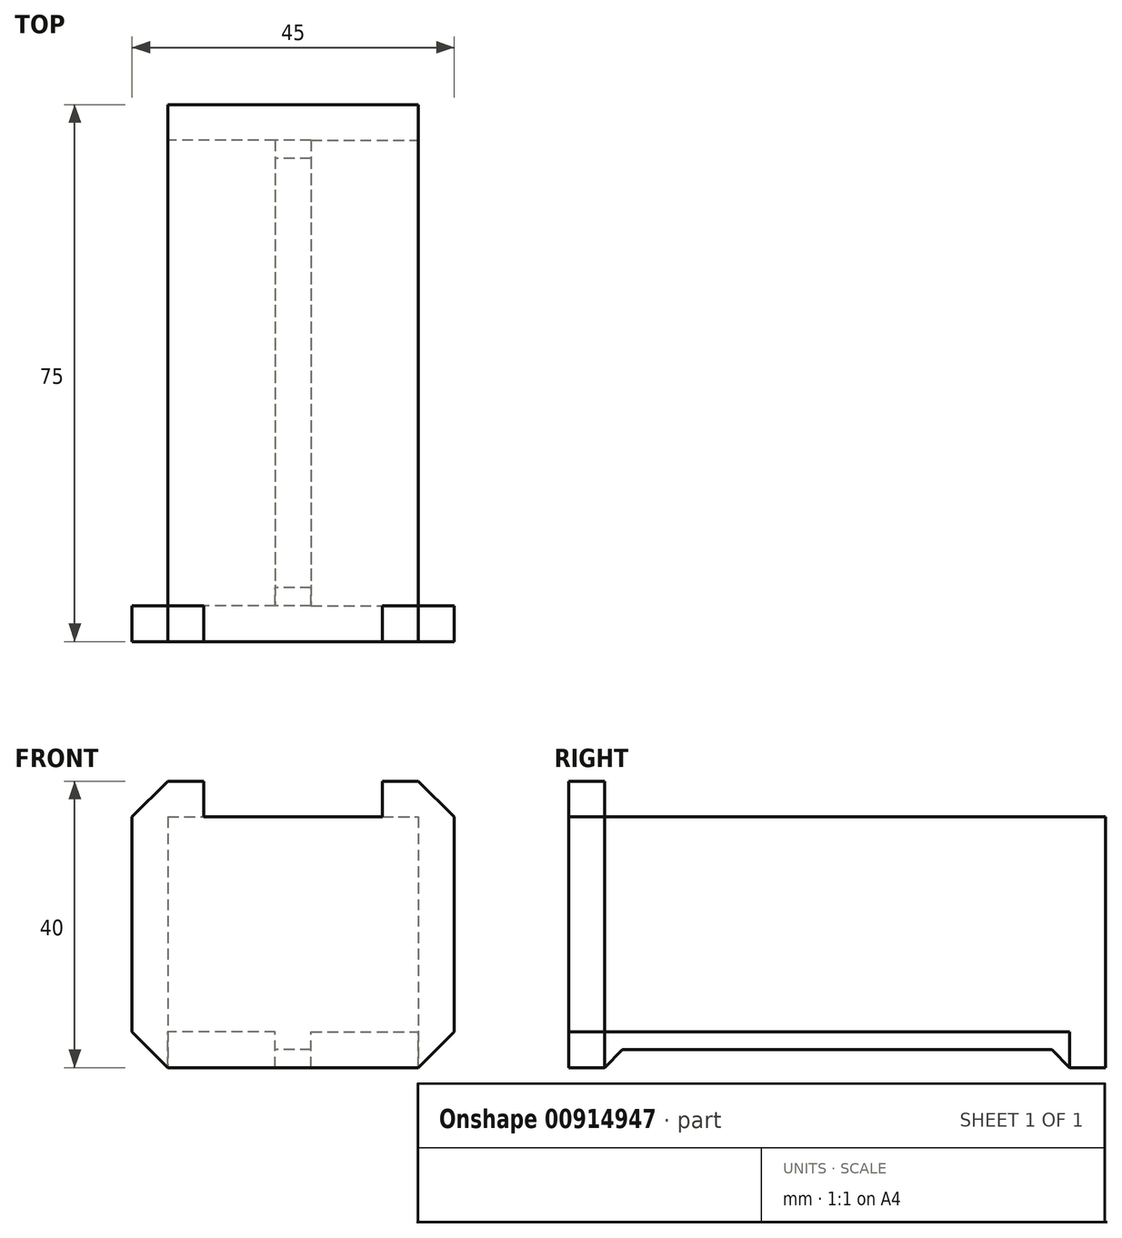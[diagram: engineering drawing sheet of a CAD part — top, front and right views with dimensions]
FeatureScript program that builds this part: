
annotation { "Feature Type Name" : "Feature", "Feature Type Description" : "" }
export const myFeature = defineFeature(function(context is Context, id is Id, definition is map)
    precondition{}
    {
        {
            var Q0;
            Q0=qCreatedBy(makeId("Top.planeOp"),FACE);
            var sketch = newSketch(context, id + "F0", { "sketchPlane" : qUnion([Q0])});
            skLineSegment(sketch, "E0", {"start": v(0, 0) * mm, "end": v(17.5, 0) * mm});
            skLineSegment(sketch, "E1.MirrorCS", {"start": v(0, 0) * mm, "end": v(-17.5, 0) * mm});
            skLineSegment(sketch, "E2", {"start": v(-17.5, 37.5) * mm, "end": v(-17.5, -37.5) * mm});
            skLineSegment(sketch, "E3.MirrorCS", {"start": v(17.5, 37.5) * mm, "end": v(17.5, -37.5) * mm});
            skLineSegment(sketch, "E4", {"start": v(-17.5, -37.5) * mm, "end": v(17.5, -37.5) * mm});
            skLineSegment(sketch, "E5", {"start": v(-17.5, 37.5) * mm, "end": v(17.5, 37.5) * mm});
            skLineSegment(sketch, "E6", {"start": v(0, 37.5) * mm, "end": v(-2.5, 37.5) * mm});
            skLineSegment(sketch, "E7", {"start": v(-2.5, 37.5) * mm, "end": v(-2.5, -37.5) * mm});
            skLineSegment(sketch, "E8.MirrorCS", {"start": v(2.5, 37.5) * mm, "end": v(2.5, -37.5) * mm});
            skLineSegment(sketch, "E9", {"start": v(2.5, 32.5) * mm, "end": v(-2.5, 32.5) * mm});
            skLineSegment(sketch, "E10", {"start": v(-17.5, -37.5) * mm, "end": v(-22.5, -37.5) * mm});
            skLineSegment(sketch, "E11.MirrorCS", {"start": v(2.5, -32.5) * mm, "end": v(-2.5, -32.5) * mm});
            skLineSegment(sketch, "E12", {"start": v(-2.5, -32.5) * mm, "end": v(-22.5, -32.5) * mm});
            skLineSegment(sketch, "E13", {"start": v(-22.5, -32.5) * mm, "end": v(-22.5, -37.5) * mm});
            skLineSegment(sketch, "E14.MirrorCS", {"start": v(2.5, -32.5) * mm, "end": v(22.5, -32.5) * mm});
            skLineSegment(sketch, "E15.MirrorCS", {"start": v(22.5, -32.5) * mm, "end": v(22.5, -37.5) * mm});
            skLineSegment(sketch, "E16.MirrorCS", {"start": v(17.5, -37.5) * mm, "end": v(22.5, -37.5) * mm});
            skLineSegment(sketch, "E17.MirrorCS", {"start": v(-2.5, 32.5) * mm, "end": v(-22.5, 32.5) * mm});
            skLineSegment(sketch, "E18.MirrorCS", {"start": v(-22.5, 32.5) * mm, "end": v(-22.5, 37.5) * mm});
            skLineSegment(sketch, "E19.MirrorCS", {"start": v(-17.5, 37.5) * mm, "end": v(-22.5, 37.5) * mm});
            skLineSegment(sketch, "E20.MirrorCS", {"start": v(2.5, 32.5) * mm, "end": v(22.5, 32.5) * mm});
            skLineSegment(sketch, "E21.MirrorCS", {"start": v(17.5, 37.5) * mm, "end": v(22.5, 37.5) * mm});
            skLineSegment(sketch, "E22.MirrorCS", {"start": v(22.5, 32.5) * mm, "end": v(22.5, 37.5) * mm});
            skSolve(sketch);
        }
        {
            var Q0;
            {var subQ3=sQuery(id+"F0.wireOp",EDGE,"E1.MirrorCS");Q0=makeQuery(id+"F0.imprint","IMPRINT",FACE,{"disambiguationData":[TD([[makeQuery(id+"F0.imprint","IMPRINT",EDGE,{"derivedFrom":subQ3}),-1.0]])]});}
            var Q1;
            {var subQ3=sQuery(id+"F0.wireOp",EDGE,"E1.MirrorCS");Q1=makeQuery(id+"F0.imprint","IMPRINT",FACE,{"disambiguationData":[TD([[makeQuery(id+"F0.imprint","IMPRINT",EDGE,{"derivedFrom":subQ3}),1.0]])]});}
            var Q2;
            {var subQ3=sQuery(id+"F0.wireOp",EDGE,"E0");Q2=makeQuery(id+"F0.imprint","IMPRINT",FACE,{"disambiguationData":[TD([[makeQuery(id+"F0.imprint","IMPRINT",EDGE,{"derivedFrom":subQ3}),1.0]])]});}
            var Q3;
            {var subQ3=sQuery(id+"F0.wireOp",EDGE,"E0");Q3=makeQuery(id+"F0.imprint","IMPRINT",FACE,{"disambiguationData":[TD([[makeQuery(id+"F0.imprint","IMPRINT",EDGE,{"derivedFrom":subQ3}),-1.0]])]});}
            var Q4;
            {var subQ0=sQuery(id+"F0.wireOp",EDGE,"E6");Q4=makeQuery(id+"F0.imprint","IMPRINT",FACE,{"disambiguationData":[TD([[makeQuery(id+"F0.imprint","IMPRINT",EDGE,{"derivedFrom":subQ0}),1.0]])]});}
            var Q5;
            {var subQ3=sQuery(id+"F0.wireOp",EDGE,"E1.MirrorCS");var subQ7=sQuery(id+"F0.wireOp",EDGE,"E0");var subQ8=makeQuery(id+"F0.imprint","INTERSECT",VERTEX,{"derivedFrom":[subQ7,subQ3]});Q5=makeQuery(id+"F0.imprint","IMPRINT",FACE,{"disambiguationData":[TD([[makeQuery(id+"F0.imprint","IMPRINT",EDGE,{"disambiguationData":[TD([[subQ8,-1.0]])],"derivedFrom":subQ7}),-1.0]])]});}
            var Q6;
            {var subQ2=sQuery(id+"F0.wireOp",EDGE,"E1.MirrorCS");var subQ4=sQuery(id+"F0.wireOp",EDGE,"E0");var subQ5=makeQuery(id+"F0.imprint","INTERSECT",VERTEX,{"derivedFrom":[subQ4,subQ2]});Q6=makeQuery(id+"F0.imprint","IMPRINT",FACE,{"disambiguationData":[TD([[makeQuery(id+"F0.imprint","IMPRINT",EDGE,{"disambiguationData":[TD([[subQ5,-1.0]])],"derivedFrom":subQ4}),1.0]])]});}
            var Q7;
            {var subQ0=sQuery(id+"F0.wireOp",EDGE,"E5");var subQ5=sQuery(id+"F0.wireOp",EDGE,"E8.MirrorCS");var subQ6=makeQuery(id+"F0.imprint","INTERSECT",VERTEX,{"derivedFrom":[subQ5,subQ0]});Q7=makeQuery(id+"F0.imprint","IMPRINT",FACE,{"disambiguationData":[TD([[makeQuery(id+"F0.imprint","IMPRINT",EDGE,{"disambiguationData":[TD([[subQ6,-1.0]])],"derivedFrom":subQ5}),1.0]])]});}
            var Q8;
            {var subQ0=sQuery(id+"F0.wireOp",EDGE,"E5");var subQ5=sQuery(id+"F0.wireOp",EDGE,"E7");var subQ6=makeQuery(id+"F0.imprint","INTERSECT",VERTEX,{"derivedFrom":[subQ5,subQ0]});Q8=makeQuery(id+"F0.imprint","IMPRINT",FACE,{"disambiguationData":[TD([[makeQuery(id+"F0.imprint","IMPRINT",EDGE,{"disambiguationData":[TD([[subQ6,-1.0]])],"derivedFrom":subQ5}),-1.0]])]});}
            var Q9;
            {var subQ0=sQuery(id+"F0.wireOp",EDGE,"E4");var subQ5=sQuery(id+"F0.wireOp",EDGE,"E8.MirrorCS");var subQ6=makeQuery(id+"F0.imprint","INTERSECT",VERTEX,{"derivedFrom":[subQ0,subQ5]});Q9=makeQuery(id+"F0.imprint","IMPRINT",FACE,{"disambiguationData":[TD([[makeQuery(id+"F0.imprint","IMPRINT",EDGE,{"disambiguationData":[TD([[subQ6,1.0]])],"derivedFrom":subQ5}),1.0]])]});}
            var Q10;
            {var subQ0=sQuery(id+"F0.wireOp",EDGE,"E4");var subQ5=sQuery(id+"F0.wireOp",EDGE,"E7");var subQ6=makeQuery(id+"F0.imprint","INTERSECT",VERTEX,{"derivedFrom":[subQ0,subQ5]});Q10=makeQuery(id+"F0.imprint","IMPRINT",FACE,{"disambiguationData":[TD([[makeQuery(id+"F0.imprint","IMPRINT",EDGE,{"disambiguationData":[TD([[subQ6,1.0]])],"derivedFrom":subQ5}),-1.0]])]});}
            var Q11;
            {var subQ5=sQuery(id+"F0.wireOp",EDGE,"dEvHe9y1-2jJR-No0K-y1cl-9SdO0pkzURjJ");Q11=makeQuery(id+"F0.imprint","IMPRINT",FACE,{"disambiguationData":[TD([[makeQuery(id+"F0.imprint","IMPRINT",EDGE,{"derivedFrom":subQ5}),1.0]])]});}
            var Q12;
            {var subQ3=sQuery(id+"F0.wireOp",EDGE,"E9");Q12=makeQuery(id+"F0.imprint","IMPRINT",FACE,{"disambiguationData":[TD([[makeQuery(id+"F0.imprint","IMPRINT",EDGE,{"derivedFrom":subQ3}),-1.0]])]});}
            var Q13;
            {var subQ5=sQuery(id+"F0.wireOp",EDGE,"E11.MirrorCS");Q13=makeQuery(id+"F0.imprint","IMPRINT",FACE,{"disambiguationData":[TD([[makeQuery(id+"F0.imprint","IMPRINT",EDGE,{"derivedFrom":subQ5}),1.0]])]});}
            extrude(context, id + "F1", {"entities" : qUnion([Q0, Q1, Q2, Q3, Q4, Q5, Q6, Q7, Q8, Q9, Q10, Q11, Q12, Q13]), "depth" : 30 * mm, "offsetDistance" : 25 * mm});
        }
        {
            var Q0;
            {var subQ1=sQuery(id+"F0.wireOp",EDGE,"E2");var subQ3=sQuery(id+"F0.wireOp",EDGE,"E12");var subQ4=makeQuery(id+"F0.imprint","INTERSECT",VERTEX,{"derivedFrom":[subQ1,subQ3]});Q0=makeQuery(id+"F0.imprint","IMPRINT",FACE,{"disambiguationData":[TD([[makeQuery(id+"F0.imprint","IMPRINT",EDGE,{"disambiguationData":[TD([[subQ4,-1.0]])],"derivedFrom":subQ1}),1.0]])]});}
            var Q1;
            {var subQ1=sQuery(id+"F0.wireOp",EDGE,"E2");var subQ3=sQuery(id+"F0.wireOp",EDGE,"E17.MirrorCS");var subQ4=makeQuery(id+"F0.imprint","INTERSECT",VERTEX,{"derivedFrom":[subQ1,subQ3]});Q1=makeQuery(id+"F0.imprint","IMPRINT",FACE,{"disambiguationData":[TD([[makeQuery(id+"F0.imprint","IMPRINT",EDGE,{"disambiguationData":[TD([[subQ4,1.0]])],"derivedFrom":subQ1}),1.0]])]});}
            var Q2;
            {var subQ1=sQuery(id+"F0.wireOp",EDGE,"E3.MirrorCS");var subQ3=sQuery(id+"F0.wireOp",EDGE,"E14.MirrorCS");var subQ4=makeQuery(id+"F0.imprint","INTERSECT",VERTEX,{"derivedFrom":[subQ1,subQ3]});Q2=makeQuery(id+"F0.imprint","IMPRINT",FACE,{"disambiguationData":[TD([[makeQuery(id+"F0.imprint","IMPRINT",EDGE,{"disambiguationData":[TD([[subQ4,-1.0]])],"derivedFrom":subQ1}),-1.0]])]});}
            var Q3;
            {var subQ0=sQuery(id+"F0.wireOp",EDGE,"E9");Q3=makeQuery(id+"F0.imprint","IMPRINT",FACE,{"disambiguationData":[TD([[makeQuery(id+"F0.imprint","IMPRINT",EDGE,{"derivedFrom":subQ0}),1.0]])]});}
            var Q4;
            {var subQ1=sQuery(id+"F0.wireOp",EDGE,"E3.MirrorCS");var subQ3=sQuery(id+"F0.wireOp",EDGE,"E20.MirrorCS");var subQ4=makeQuery(id+"F0.imprint","INTERSECT",VERTEX,{"derivedFrom":[subQ1,subQ3]});Q4=makeQuery(id+"F0.imprint","IMPRINT",FACE,{"disambiguationData":[TD([[makeQuery(id+"F0.imprint","IMPRINT",EDGE,{"disambiguationData":[TD([[subQ4,1.0]])],"derivedFrom":subQ1}),-1.0]])]});}
            var Q5;
            {var subQ3=sQuery(id+"F0.wireOp",EDGE,"E9");Q5=makeQuery(id+"F0.imprint","IMPRINT",FACE,{"disambiguationData":[TD([[makeQuery(id+"F0.imprint","IMPRINT",EDGE,{"derivedFrom":subQ3}),-1.0]])]});}
            var Q6;
            {var subQ0=sQuery(id+"F0.wireOp",EDGE,"E11.MirrorCS");Q6=makeQuery(id+"F0.imprint","IMPRINT",FACE,{"disambiguationData":[TD([[makeQuery(id+"F0.imprint","IMPRINT",EDGE,{"derivedFrom":subQ0}),-1.0]])]});}
            var Q7;
            {var subQ5=sQuery(id+"F0.wireOp",EDGE,"E11.MirrorCS");Q7=makeQuery(id+"F0.imprint","IMPRINT",FACE,{"disambiguationData":[TD([[makeQuery(id+"F0.imprint","IMPRINT",EDGE,{"derivedFrom":subQ5}),1.0]])]});}
            var Q8;
            {var subQ4=sQuery(id+"F0.wireOp",EDGE,"E15.MirrorCS");Q8=makeQuery(id+"F0.imprint","IMPRINT",FACE,{"disambiguationData":[TD([[makeQuery(id+"F0.imprint","IMPRINT",EDGE,{"derivedFrom":subQ4}),-1.0]])]});}
            var Q9;
            {var subQ0=sQuery(id+"F0.wireOp",EDGE,"E10");Q9=makeQuery(id+"F0.imprint","IMPRINT",FACE,{"disambiguationData":[TD([[makeQuery(id+"F0.imprint","IMPRINT",EDGE,{"derivedFrom":subQ0}),-1.0]])]});}
            extrude(context, id + "F2", {"entities" : qUnion([Q0, Q1, Q2, Q3, Q4, Q5, Q6, Q7, Q8, Q9]), "oppositeDirection" : true, "depth" : 5 * mm, "offsetDistance" : 25 * mm});
        }
        {
            var Q0;
            {var subQ0=sQuery(id+"F0.wireOp",EDGE,"E10");Q0=makeQuery(id+"F0.imprint","IMPRINT",FACE,{"disambiguationData":[TD([[makeQuery(id+"F0.imprint","IMPRINT",EDGE,{"derivedFrom":subQ0}),-1.0]])]});}
            var Q1;
            {var subQ4=sQuery(id+"F0.wireOp",EDGE,"E15.MirrorCS");Q1=makeQuery(id+"F0.imprint","IMPRINT",FACE,{"disambiguationData":[TD([[makeQuery(id+"F0.imprint","IMPRINT",EDGE,{"derivedFrom":subQ4}),-1.0]])]});}
            extrude(context, id + "F3", {"entities" : qUnion([Q0, Q1]), "operationType" : NewBodyOperationType.ADD, "depth" : 35 * mm, "offsetDistance" : 25 * mm});
        }
        {
            var Q0;
            {var subQ0=sQuery(id+"F0.wireOp",EDGE,"E16.MirrorCS");var subQ1=sQuery(id+"F0.wireOp",EDGE,"E10");Q0=makeQuery(id+"F3.boolean.opBoolean","MERGE",FACE,{"derivedFrom":[makeQuery(id+"F2.opExtrude","SWEPT_FACE",FACE,{"disambiguationData":[OSD([sQuery(id+"F0.wireOp",EDGE,"E4"),subQ1,subQ0])]}),makeQuery(id+"F3.opExtrude","SWEPT_FACE",FACE,{"disambiguationData":[OSD([subQ1])]}),makeQuery(id+"F3.opExtrude","SWEPT_FACE",FACE,{"disambiguationData":[OSD([subQ0])]})]});}
            var sketch = newSketch(context, id + "F4", { "sketchPlane" : qUnion([Q0])});
            skLineSegment(sketch, "E23", {"start": v(-17.5, 35) * mm, "end": v(-12.5, 35) * mm});
            skLineSegment(sketch, "E24", {"start": v(-17.5, 35) * mm, "end": v(-17.5, 30) * mm});
            skLineSegment(sketch, "E25", {"start": v(-17.5, 30) * mm, "end": v(-12.5, 30) * mm});
            skLineSegment(sketch, "E26", {"start": v(-12.5, 35) * mm, "end": v(-12.5, 30) * mm});
            skLineSegment(sketch, "E27.MirrorCS", {"start": v(12.5, 35) * mm, "end": v(12.5, 30) * mm});
            skLineSegment(sketch, "E28.MirrorCS", {"start": v(17.5, 35) * mm, "end": v(12.5, 35) * mm});
            skLineSegment(sketch, "E29.MirrorCS", {"start": v(17.5, 30) * mm, "end": v(12.5, 30) * mm});
            skLineSegment(sketch, "E30.MirrorCS", {"start": v(17.5, 35) * mm, "end": v(17.5, 30) * mm});
            skSolve(sketch);
        }
        {
            var Q0;
            Q0=makeQuery(id+"F4.imprint","IMPRINT",FACE,{"disambiguationData":[TD([[makeQuery(id+"F4.imprint","IMPRINT",EDGE,{"derivedFrom":sQuery(id+"F4.wireOp",EDGE,"E23")}),-1.0]])]});
            var Q1;
            Q1=makeQuery(id+"F4.imprint","IMPRINT",FACE,{"disambiguationData":[TD([[makeQuery(id+"F4.imprint","IMPRINT",EDGE,{"derivedFrom":sQuery(id+"F4.wireOp",EDGE,"E27.MirrorCS")}),1.0]])]});
            extrude(context, id + "F5", {"entities" : qUnion([Q0, Q1]), "operationType" : NewBodyOperationType.ADD, "oppositeDirection" : true, "depth" : 5 * mm, "offsetDistance" : 25 * mm});
        }
        {
            var Q0;
            Q0=makeQuery(id+"F2.opExtrude","SWEPT_FACE",FACE,{"disambiguationData":[OSD([sQuery(id+"F0.wireOp",EDGE,"E7")])]});
            var sketch = newSketch(context, id + "F6", { "sketchPlane" : qUnion([Q0])});
            skLineSegment(sketch, "E31", {"start": v(-32.5, -5) * mm, "end": v(-32.5, -2.5) * mm});
            skLineSegment(sketch, "E32", {"start": v(-32.5, -2.5) * mm, "end": v(32.5, -2.5) * mm});
            skLineSegment(sketch, "E33", {"start": v(32.5, -2.5) * mm, "end": v(30, -2.5) * mm});
            skLineSegment(sketch, "E34", {"start": v(32.5, -5) * mm, "end": v(30, -2.5) * mm});
            skLineSegment(sketch, "E35.MirrorCS", {"start": v(-32.5, -5) * mm, "end": v(-30, -2.5) * mm});
            skLineSegment(sketch, "E36", {"start": v(32.5, -2.5) * mm, "end": v(32.5, -5) * mm});
            skSolve(sketch);
        }
        {
            var Q0;
            {var subQ0=sQuery(id+"F6.wireOp",EDGE,"E34");Q0=makeQuery(id+"F6.imprint","IMPRINT",FACE,{"disambiguationData":[TD([[makeQuery(id+"F6.imprint","IMPRINT",EDGE,{"derivedFrom":subQ0}),1.0]])]});}
            extrude(context, id + "F7", {"entities" : qUnion([Q0]), "operationType" : NewBodyOperationType.REMOVE, "oppositeDirection" : true, "depth" : 5 * mm, "offsetDistance" : 25 * mm});
        }
        {
            var Q0;
            {var subQ0=sQuery(id+"F0.wireOp",EDGE,"E16.MirrorCS");var subQ1=sQuery(id+"F0.wireOp",EDGE,"E10");Q0=makeQuery(id+"F5.boolean.opBoolean","MERGE",FACE,{"derivedFrom":[makeQuery(id+"F3.boolean.opBoolean","MERGE",FACE,{"derivedFrom":[makeQuery(id+"F2.opExtrude","SWEPT_FACE",FACE,{"disambiguationData":[OSD([sQuery(id+"F0.wireOp",EDGE,"E4"),subQ1,subQ0])]}),makeQuery(id+"F3.opExtrude","SWEPT_FACE",FACE,{"disambiguationData":[OSD([subQ1])]}),makeQuery(id+"F3.opExtrude","SWEPT_FACE",FACE,{"disambiguationData":[OSD([subQ0])]})]}),makeQuery(id+"F5.opExtrude","CAP_FACE",FACE,{"disambiguationData":[OSD([sQuery(id+"F4.wireOp",EDGE,"E23"),sQuery(id+"F4.wireOp",EDGE,"E24"),sQuery(id+"F4.wireOp",EDGE,"E25"),sQuery(id+"F4.wireOp",EDGE,"E26")])],"isStart":true}),makeQuery(id+"F5.opExtrude","CAP_FACE",FACE,{"disambiguationData":[OSD([sQuery(id+"F4.wireOp",EDGE,"E27.MirrorCS"),sQuery(id+"F4.wireOp",EDGE,"E28.MirrorCS"),sQuery(id+"F4.wireOp",EDGE,"E29.MirrorCS"),sQuery(id+"F4.wireOp",EDGE,"E30.MirrorCS")])],"isStart":true})]});}
            var sketch = newSketch(context, id + "F8", { "sketchPlane" : qUnion([Q0])});
            skLineSegment(sketch, "E37", {"start": v(-22.5, 0) * mm, "end": v(-17.5, -5) * mm});
            skLineSegment(sketch, "E38.MirrorCS", {"start": v(22.5, 0) * mm, "end": v(17.5, -5) * mm});
            skLineSegment(sketch, "E39", {"start": v(-22.5, 0) * mm, "end": v(-22.5, -5) * mm});
            skLineSegment(sketch, "E40", {"start": v(-22.5, -5) * mm, "end": v(-17.5, -5) * mm});
            skLineSegment(sketch, "E41", {"start": v(17.5, -5) * mm, "end": v(22.5, -5) * mm});
            skLineSegment(sketch, "E42", {"start": v(22.5, 0) * mm, "end": v(22.5, -5) * mm});
            skLineSegment(sketch, "E43", {"start": v(-22.5, -5) * mm, "end": v(-22.5, 35) * mm});
            skLineSegment(sketch, "E44.MirrorCS", {"start": v(-22.5, 30) * mm, "end": v(-17.5, 35) * mm});
            skLineSegment(sketch, "E45.MirrorCS", {"start": v(22.5, 30) * mm, "end": v(17.5, 35) * mm});
            skSolve(sketch);
        }
        {
            var Q0;
            {var subQ3=sQuery(id+"F8.wireOp",EDGE,"E44.MirrorCS");Q0=makeQuery(id+"F8.imprint","IMPRINT",FACE,{"disambiguationData":[TD([[makeQuery(id+"F8.imprint","IMPRINT",EDGE,{"derivedFrom":subQ3}),1.0]])]});}
            var Q1;
            {var subQ0=sQuery(id+"F8.wireOp",EDGE,"E45.MirrorCS");Q1=makeQuery(id+"F8.imprint","IMPRINT",FACE,{"disambiguationData":[TD([[makeQuery(id+"F8.imprint","IMPRINT",EDGE,{"derivedFrom":subQ0}),-1.0]])]});}
            var Q2;
            {var subQ0=sQuery(id+"F8.wireOp",EDGE,"E37");Q2=makeQuery(id+"F8.imprint","IMPRINT",FACE,{"disambiguationData":[TD([[makeQuery(id+"F8.imprint","IMPRINT",EDGE,{"derivedFrom":subQ0}),-1.0]])]});}
            var Q3;
            Q3=makeQuery(id+"F8.imprint","IMPRINT",FACE,{"disambiguationData":[TD([[makeQuery(id+"F8.imprint","IMPRINT",EDGE,{"derivedFrom":sQuery(id+"F8.wireOp",EDGE,"E38.MirrorCS")}),1.0]])]});
            extrude(context, id + "F9", {"entities" : qUnion([Q0, Q1, Q2, Q3]), "operationType" : NewBodyOperationType.REMOVE, "oppositeDirection" : true, "depth" : 75 * mm, "offsetDistance" : 25 * mm});
        }
    });
